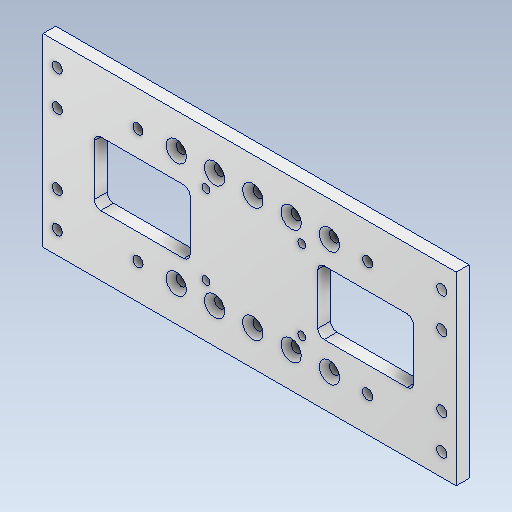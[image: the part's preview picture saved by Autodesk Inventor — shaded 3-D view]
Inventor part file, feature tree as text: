
AUTODESK INVENTOR PART (.ipt)
format: ipt  version: 2020.5 (Build 245400000, 400)  size: 319,488 bytes
history: native  units: mm
features: extrude x6, sketch x6, other x1, chamfer x1, projected_geometry x1
ambient origin geometry x8: Origin, YZ Plane, XZ Plane, XY Plane, X Axis, Y Axis, Z Axis, Center Point
bodies: Body1 (feature_tree)
feature tree (15):
  other  "솔리드1"
  extrude  "돌출1"  Depth=58.0mm
  extrude  "돌출2"  Depth=129.5mm
  extrude  "돌출3"  Depth=4.0mm TaperAngle=0.0deg
  extrude  "돌출4"  Depth=6.0mm TaperAngle=0.0deg
  extrude  "돌출5"  Depth=4.0mm TaperAngle=0.0deg
  extrude  "돌출6"  Depth=4.5mm
  chamfer  "모따기1"  Distance=3.2mm
  sketch  "스케치1"
  sketch  "스케치2"
  sketch  "스케치3"
  projected_geometry  "투영된 루프1"
  sketch  "스케치4"
  sketch  "스케치5"
  sketch  "스케치6"
